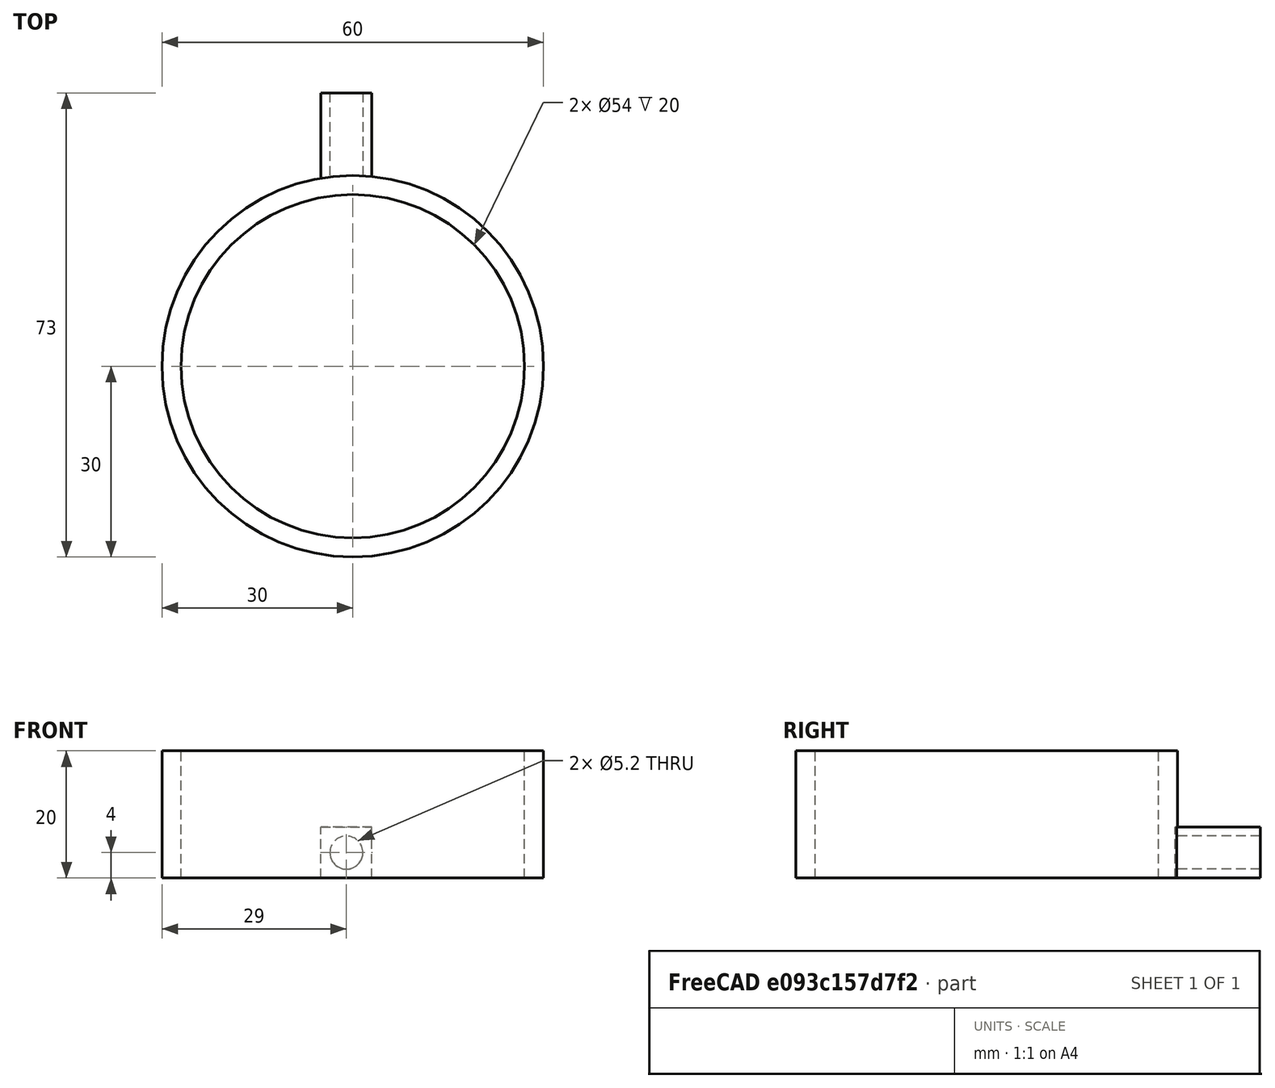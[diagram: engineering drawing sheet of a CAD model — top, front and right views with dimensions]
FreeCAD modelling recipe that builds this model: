
FCSTD DOCUMENT  (FreeCAD 0.16R6712 (Git))
Label: i-seasons4
License: All rights reserved
LicenseURL: http://en.wikipedia.org/wiki/All_rights_reserved
objects: Part::Cylinder×3, Part::Cut×2, Part::Box×1, Part::MultiFuse×1, Part::Feature×1
note: 8 computed .brp shape members not serialized (recipe doc carries the construction recipe); baked Part::Feature solids carry a one-line shape summary decoded from their .brp

FEATURE [Part::Cylinder] Cylinder  label="Cylinder outside"
  Angle = 360
  Height = 20
  Radius = 30
FEATURE [Part::Cylinder] Cylinder001  label="Cylinder inside"
  Angle = 360
  Height = 20
  Radius = 27
FEATURE [Part::Cylinder] Cylinder002  label="straw hole"
  Angle = 360
  Height = 15
  Placement = pos=(-1,30,4) rot=(1,0,0;1.5708rad)
  Radius = 2.6
FEATURE [Part::Cut] Cut
  Base = -> Cylinder
  Tool = -> Cylinder001
FEATURE [Part::Box] Box  label="strow cube"
  Height = 8
  Length = 8
  Placement = pos=(-5,15,0) rot=(0,0,1;0rad)
  Width = 15
FEATURE [Part::Cut] Cut001
  Base = -> Box
  Placement = pos=(0,13,0) rot=(0,0,1;0rad)
  Tool = -> Cylinder002
FEATURE [Part::MultiFuse] Fusion
  Shapes = -> [Cut001,Cut]
FEATURE [Part::Feature] Fusion001  label="piece to print"
  shape: bbox 60 x 73 x 20 mm, 10 faces (baked)
